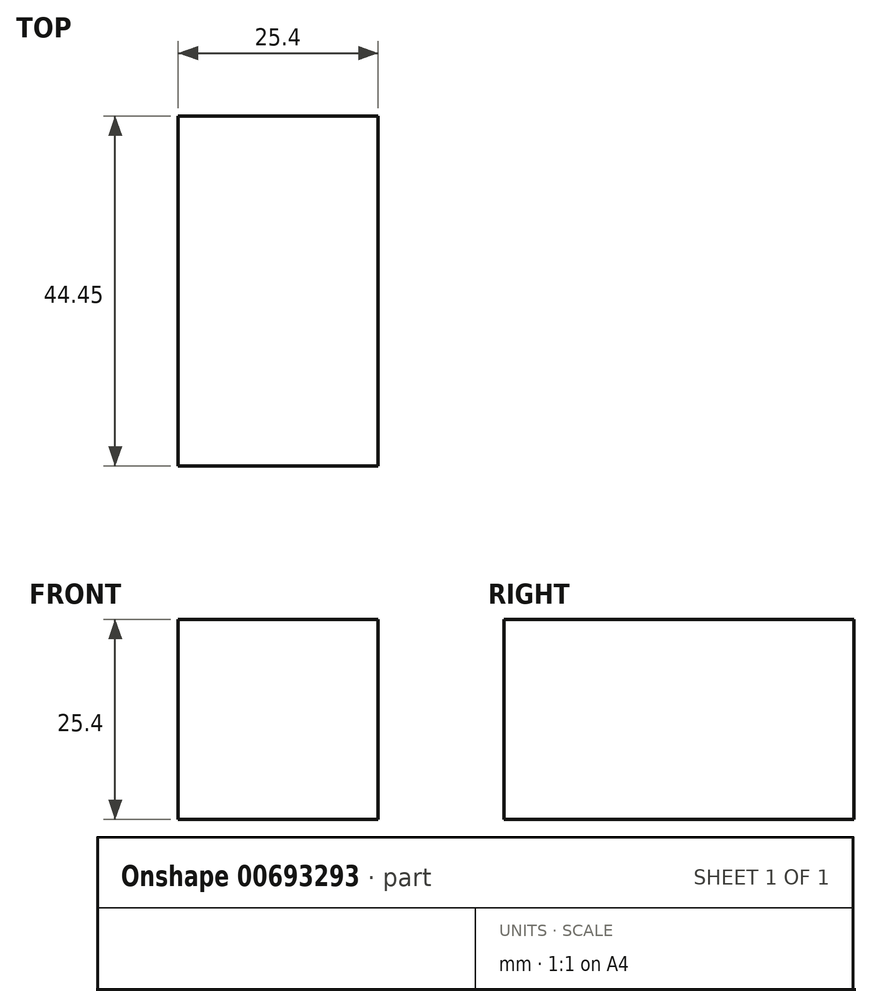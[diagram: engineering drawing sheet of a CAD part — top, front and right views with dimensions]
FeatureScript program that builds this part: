
annotation { "Feature Type Name" : "Feature", "Feature Type Description" : "" }
export const myFeature = defineFeature(function(context is Context, id is Id, definition is map)
    precondition{}
    {
        {
            var Q0;
            Q0=qCreatedBy(makeId("Right.planeOp"),FACE);
            var sketch = newSketch(context, id + "F0", { "sketchPlane" : qUnion([Q0])});
            skLineSegment(sketch, "E0.bottom", {"start": v(0, 0) * mm, "end": v(-44.45, 0) * mm});
            skLineSegment(sketch, "E0.top", {"start": v(0, 25.4) * mm, "end": v(-44.45, 25.4) * mm});
            skLineSegment(sketch, "E0.left", {"start": v(0, 0) * mm, "end": v(0, 25.4) * mm});
            skLineSegment(sketch, "E0.right", {"start": v(-44.45, 0) * mm, "end": v(-44.45, 25.4) * mm});
            skSolve(sketch);
        }
        {
            var Q0;
            Q0=makeQuery(id+"F0.imprint","IMPRINT",FACE,{"disambiguationData":[TD([[makeQuery(id+"F0.imprint","IMPRINT",EDGE,{"derivedFrom":sQuery(id+"F0.wireOp",EDGE,"E0.bottom")}),-1.0]])]});
            extrude(context, id + "F1", {"entities" : qUnion([Q0]), "depth" : 25.4 * mm, "offsetDistance" : 25.4 * mm});
        }
    });
